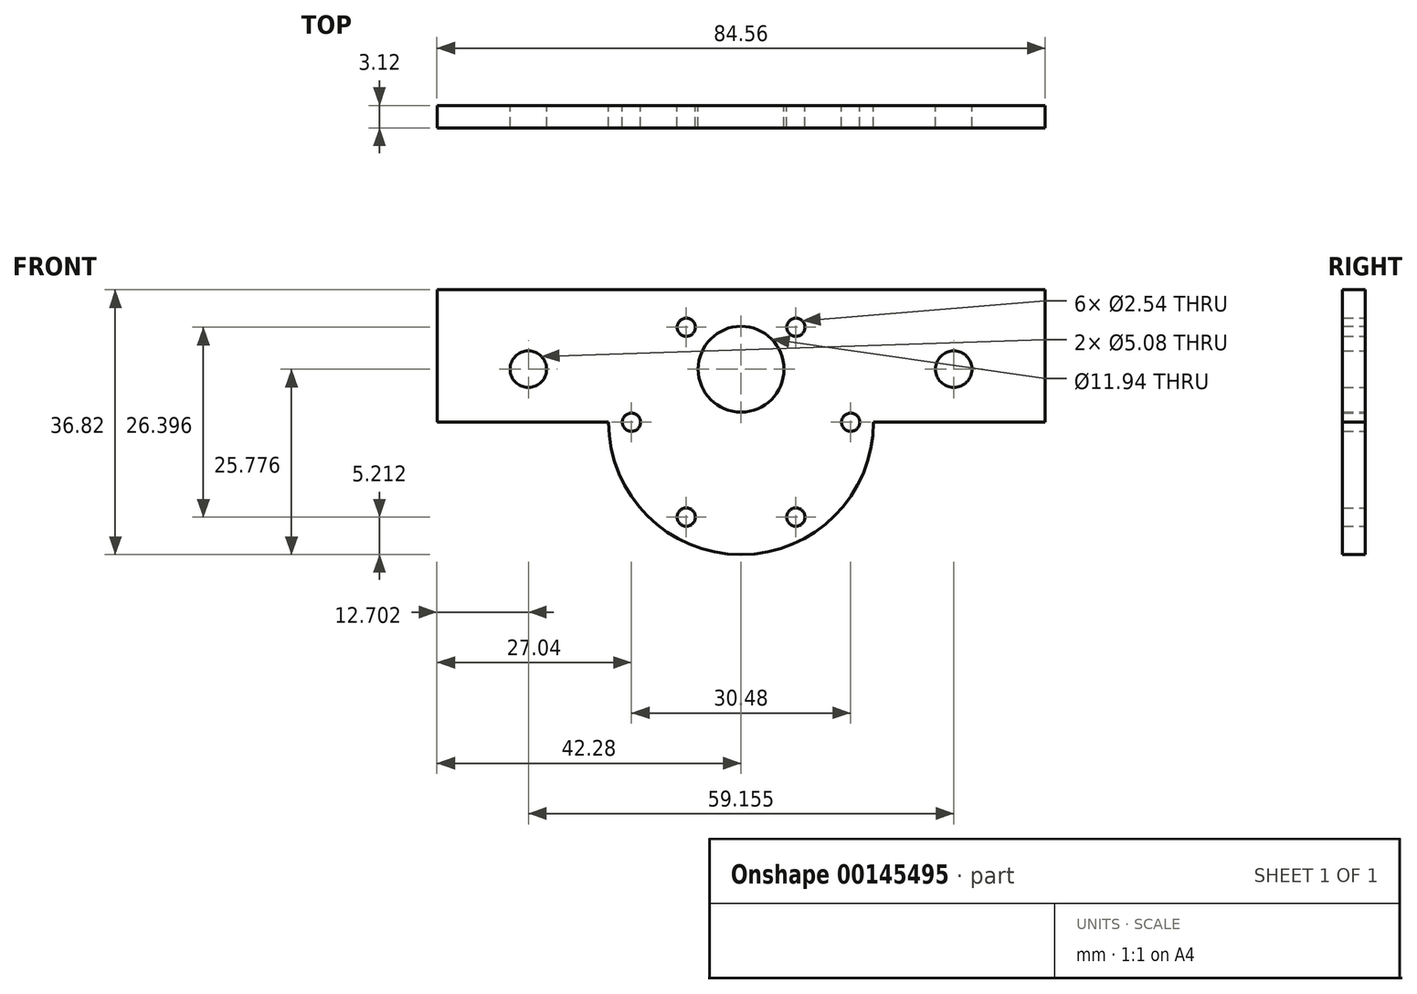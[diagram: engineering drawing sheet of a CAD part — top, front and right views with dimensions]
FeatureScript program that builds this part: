
annotation { "Feature Type Name" : "Feature", "Feature Type Description" : "" }
export const myFeature = defineFeature(function(context is Context, id is Id, definition is map)
    precondition{}
    {
        {
            var Q0;
            Q0=qCreatedBy(makeId("Front.planeOp"),FACE);
            var sketch = newSketch(context, id + "F0", { "sketchPlane" : qUnion([Q0])});
            skCircle(sketch, "E0", {"center": v(0, 0) * mm, "radius": 18.42 * mm});
            skLineSegment(sketch, "E1", {"start": v(0, 18.42) * mm, "end": v(0, 13.33) * mm, "construction": true});
            skCircle(sketch, "E2", {"center": v(0, 7.37) * mm, "radius": 5.97 * mm});
            skCircle(sketch, "E3", {"center": v(0, 7.37) * mm, "radius": 3.05 * mm});
            skCircle(sketch, "E4", {"center": v(0, 0) * mm, "radius": 15.24 * mm, "construction": true});
            skCircle(sketch, "E5", {"center": v(-15.24, 0) * mm, "radius": 1.27 * mm});
            skCircle(sketch, "E6.1.0", {"center": v(-7.62, -13.2) * mm, "radius": 1.27 * mm});
            skCircle(sketch, "E6.2.0", {"center": v(7.62, -13.2) * mm, "radius": 1.27 * mm});
            skCircle(sketch, "E6.3.0", {"center": v(15.24, 0) * mm, "radius": 1.27 * mm});
            skCircle(sketch, "E6.4.0", {"center": v(7.62, 13.2) * mm, "radius": 1.27 * mm});
            skCircle(sketch, "E6.5.0", {"center": v(-7.62, 13.2) * mm, "radius": 1.27 * mm});
            skLineSegment(sketch, "E7", {"start": v(-16.88, 7.37) * mm, "end": v(-42.28, 7.37) * mm, "construction": true});
            skLineSegment(sketch, "E8", {"start": v(16.88, 7.37) * mm, "end": v(42.28, 7.37) * mm, "construction": true});
            skLineSegment(sketch, "E9", {"start": v(-42.28, 18.41) * mm, "end": v(-42.28, 0) * mm});
            skLineSegment(sketch, "E10", {"start": v(42.28, 18.42) * mm, "end": v(42.28, 0) * mm});
            skLineSegment(sketch, "E11", {"start": v(-42.28, 0) * mm, "end": v(-18.42, 0) * mm});
            skLineSegment(sketch, "E12", {"start": v(42.28, 0) * mm, "end": v(18.42, 0) * mm});
            skLineSegment(sketch, "E13", {"start": v(-42.28, 18.41) * mm, "end": v(0, 18.42) * mm});
            skLineSegment(sketch, "E14", {"start": v(0, 18.41) * mm, "end": v(42.28, 18.41) * mm});
            skCircle(sketch, "E15", {"center": v(-29.58, 7.37) * mm, "radius": 2.54 * mm});
            skCircle(sketch, "E16", {"center": v(29.58, 7.37) * mm, "radius": 2.54 * mm});
            skSolve(sketch);
        }
        {
            var Q0;
            Q0=makeQuery(id+"F0.imprint","IMPRINT",FACE,{"disambiguationData":[TD([[makeQuery(id+"F0.imprint","IMPRINT",EDGE,{"derivedFrom":sQuery(id+"F0.wireOp",EDGE,"E0")}),1.0]])]});
            var Q1;
            Q1=makeQuery(id+"F0.imprint","IMPRINT",FACE,{"disambiguationData":[TD([[makeQuery(id+"F0.imprint","IMPRINT",EDGE,{"derivedFrom":sQuery(id+"F0.wireOp",EDGE,"E9")}),1.0]])]});
            var Q2;
            Q2=makeQuery(id+"F0.imprint","IMPRINT",FACE,{"disambiguationData":[TD([[makeQuery(id+"F0.imprint","IMPRINT",EDGE,{"derivedFrom":sQuery(id+"F0.wireOp",EDGE,"E10")}),-1.0]])]});
            extrude(context, id + "F1", {"entities" : qUnion([Q0, Q1, Q2]), "depth" : 3.12 * mm});
        }
    });
